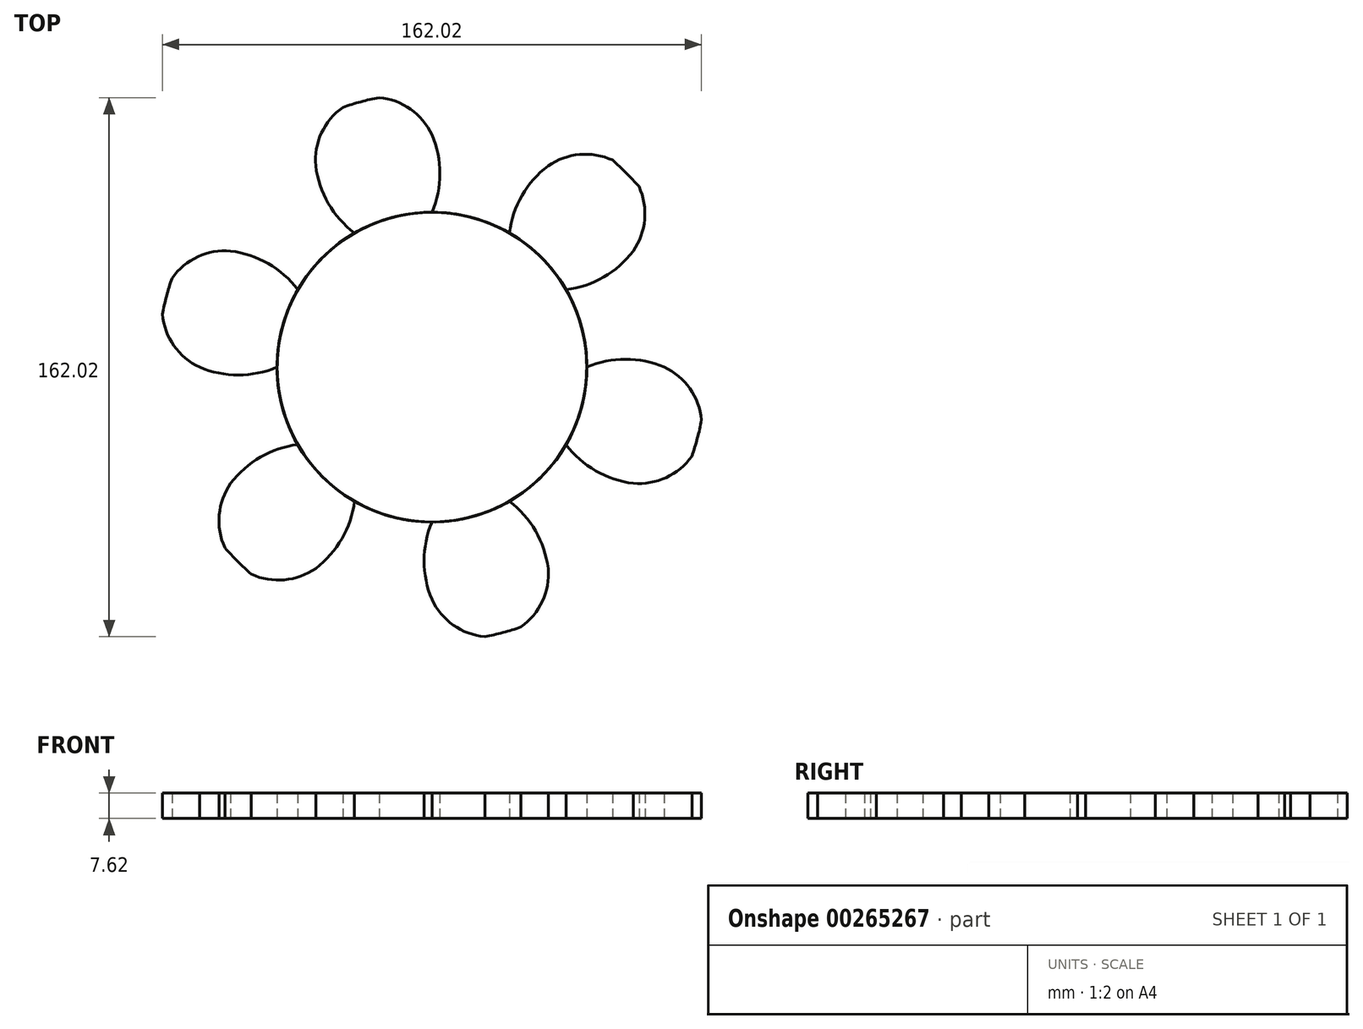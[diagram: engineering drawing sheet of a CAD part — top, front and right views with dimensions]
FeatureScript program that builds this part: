
annotation { "Feature Type Name" : "Feature", "Feature Type Description" : "" }
export const myFeature = defineFeature(function(context is Context, id is Id, definition is map)
    precondition{}
    {
        {
            var Q0;
            Q0=qCreatedBy(makeId("Top.planeOp"),FACE);
            var sketch = newSketch(context, id + "F0", { "sketchPlane" : qUnion([Q0])});
            skCircle(sketch, "E0", {"center": v(0, 0) * mm, "radius": 46.55 * mm});
            skCircle(sketch, "E1", {"center": v(0, 0) * mm, "radius": 69.82 * mm, "construction": true});
            skCircle(sketch, "E2", {"center": v(0, 0) * mm, "radius": 82.55 * mm, "construction": true});
            skLineSegment(sketch, "E3", {"start": v(0, 0) * mm, "end": v(0, 420.14) * mm, "construction": true});
            skLineSegment(sketch, "E4", {"start": v(0, 0) * mm, "end": v(-105.71, 394.52) * mm, "construction": true});
            skLineSegment(sketch, "E5", {"start": v(0, 69.82) * mm, "end": v(-381.83, 69.82) * mm, "construction": true});
            skLineSegment(sketch, "E6", {"start": v(0, 69.82) * mm, "end": v(-397.99, -75.03) * mm, "construction": true});
            skCircle(sketch, "E7", {"center": v(0, 0) * mm, "radius": 65.61 * mm, "construction": true});
            skCircle(sketch, "E8", {"center": v(0, 69.82) * mm, "radius": 17.46 * mm, "construction": true});
            skCircle(sketch, "E9", {"center": v(-16.3, 63.56) * mm, "radius": 69.82 * mm, "construction": true});
            skCircle(sketch, "E10", {"center": v(-16.3, 63.56) * mm, "radius": 17.46 * mm, "construction": true});
            skArc(sketch, "E11", {"start": v(-15.87, 81) * mm, "mid": v(-21.37, 79.74) * mm, "end": v(-26.76, 78.1) * mm});
            skArc(sketch, "E12", {"start": v(0, 69.82) * mm, "mid": v(-6.45, 77.53) * mm, "end": v(-15.87, 81) * mm});
            skArc(sketch, "E13", {"start": v(0, 46.55) * mm, "mid": v(2.36, 58.19) * mm, "end": v(0, 69.82) * mm});
            skArc(sketch, "E14.MirrorCS", {"start": v(-23.27, 40.31) * mm, "mid": v(-31.13, 49.21) * mm, "end": v(-34.91, 60.47) * mm});
            skArc(sketch, "E15.MirrorCS", {"start": v(-34.91, 60.47) * mm, "mid": v(-33.18, 70.37) * mm, "end": v(-26.76, 78.1) * mm});
            skSolve(sketch);
        }
        {
            var Q0;
            Q0=qSketchRegion(id+"F0",true);
            extrude(context, id + "F1", {"entities" : qUnion([Q0]), "depth" : 7.62 * mm});
        }
        {
            var Q0;
            Q0=makeQuery(id+"F1.opExtrude","SWEPT_BODY",BODY,{"disambiguationData":[OSD([sQuery(id+"F0.wireOp",EDGE,"E0"),sQuery(id+"F0.wireOp",EDGE,"91NiUCr4-yXFt-oEsC-2t8w-iLQuIMEs0WGp"),sQuery(id+"F0.wireOp",EDGE,"2eccd6a7-b62e-4e30-96b3-c5b5e07e5a5b0.MirrorCS"),sQuery(id+"F0.wireOp",EDGE,"SwGH1OBa-uFWg-PKz4-vmGh-Pag9Jd44Z9b1")])]});
            var Q1;
            Q1=makeQuery(id+"F1.opExtrude","SWEPT_FACE",FACE,{"disambiguationData":[OSD([sQuery(id+"F0.wireOp",EDGE,"E0")])]});
            circularPattern(context, id + "F2", {"entities" : qUnion([Q0]), "axis" : qUnion([Q1]), "angle" : 360 * degree, "instanceCount" : 6, "equalSpace" : true});
        }
    });
